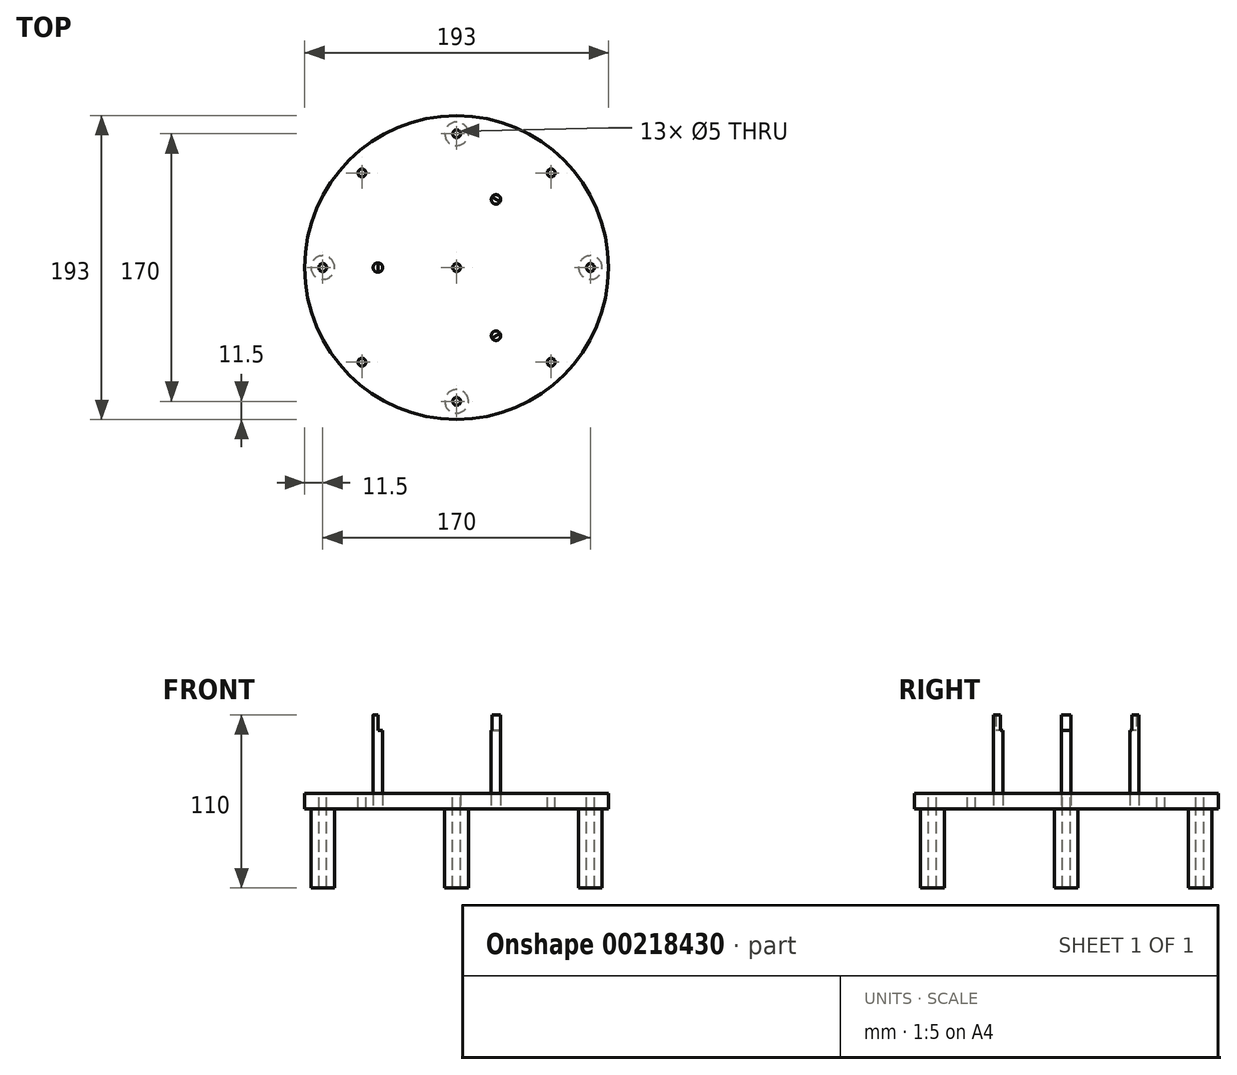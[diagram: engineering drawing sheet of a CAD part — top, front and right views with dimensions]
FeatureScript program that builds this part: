
annotation { "Feature Type Name" : "Feature", "Feature Type Description" : "" }
export const myFeature = defineFeature(function(context is Context, id is Id, definition is map)
    precondition{}
    {
        {
            var Q0;
            Q0=qCreatedBy(makeId("Front.planeOp"),FACE);
            var sketch = newSketch(context, id + "F0", { "sketchPlane" : qUnion([Q0])});
            skLineSegment(sketch, "E0", {"start": v(0, 0) * mm, "end": v(0, 66.09) * mm});
            skSolve(sketch);
        }
        {
            var Q0;
            Q0=qCreatedBy(makeId("Top.planeOp"),FACE);
            var sketch = newSketch(context, id + "F1", { "sketchPlane" : qUnion([Q0])});
            skCircle(sketch, "E1", {"center": v(0, 0) * mm, "radius": 96.5 * mm});
            skCircle(sketch, "E2.0", {"center": v(0, 0) * mm, "radius": 66.5 * mm});
            skCircle(sketch, "E3", {"center": v(0, 0) * mm, "radius": 63.5 * mm});
            skCircle(sketch, "E4", {"center": v(0, 0) * mm, "radius": 50 * mm});
            skCircle(sketch, "E5", {"center": v(0, 0) * mm, "radius": 47 * mm});
            skSolve(sketch);
        }
        {
            var Q0;
            Q0 = qSketchRegion(id + "F1", true);
            var Q1;
            Q1=makeQuery(id+"F1.imprint","IMPRINT",FACE,{"disambiguationData":[TD([[makeQuery(id+"F1.imprint","IMPRINT",EDGE,{"derivedFrom":sQuery(id+"F1.wireOp",EDGE,"E5")}),1.0]])]});
            var Q2;
            Q2=makeQuery(id+"F1.imprint","IMPRINT",FACE,{"disambiguationData":[TD([[makeQuery(id+"F1.imprint","IMPRINT",EDGE,{"derivedFrom":sQuery(id+"F1.wireOp",EDGE,"E4")}),1.0]])]});
            var Q3;
            Q3=makeQuery(id+"F1.imprint","IMPRINT",FACE,{"disambiguationData":[TD([[makeQuery(id+"F1.imprint","IMPRINT",EDGE,{"derivedFrom":sQuery(id+"F1.wireOp",EDGE,"E3")}),1.0]])]});
            var Q4;
            Q4=makeQuery(id+"F1.imprint","IMPRINT",FACE,{"disambiguationData":[TD([[makeQuery(id+"F1.imprint","IMPRINT",EDGE,{"derivedFrom":sQuery(id+"F1.wireOp",EDGE,"E2.0")}),1.0]])]});
            extrude(context, id + "F2", {"entities" : qUnion([Q0, Q1, Q2, Q3, Q4]), "depth" : 10 * mm});
        }
        {
            var Q0;
            Q0=qCreatedBy(makeId("Top.planeOp"),FACE);
            cPlane(context, id + "F3", {"entities" : qUnion([Q0]), "cplaneType" : CPlaneType.OFFSET, "offset" : 10 * mm, "width" : 150 * mm, "height" : 150 * mm});
        }
        {
            var Q0;
            Q0=qCreatedBy(id+"F3.planeOp",FACE);
            var sketch = newSketch(context, id + "F4", { "sketchPlane" : qUnion([Q0])});
            skCircle(sketch, "E6", {"center": v(-85, 0) * mm, "radius": 2.5 * mm});
            skSolve(sketch);
        }
        {
            var Q0;
            Q0=makeQuery(id+"F4.imprint","IMPRINT",FACE,{"disambiguationData":[TD([[makeQuery(id+"F4.imprint","IMPRINT",EDGE,{"derivedFrom":sQuery(id+"F4.wireOp",EDGE,"E6")}),1.0]])]});
            extrude(context, id + "F5", {"entities" : qUnion([Q0]), "oppositeDirection" : true, "depth" : 10 * mm});
        }
        {
            var Q0;
            Q0=makeQuery(id+"F5.opExtrude","SWEPT_BODY",BODY,{"disambiguationData":[OSD([sQuery(id+"F4.wireOp",EDGE,"E6")])]});
            var Q1;
            Q1=sQuery(id+"F0.wireOp",EDGE,"E0");
            circularPattern(context, id + "F6", {"entities" : qUnion([Q0]), "axis" : qUnion([Q1]), "angle" : 360 * degree, "instanceCount" : 8, "equalSpace" : true});
        }
        {
            var Q0;
            Q0=makeQuery(id+"F5.opExtrude","SWEPT_BODY",BODY,{"disambiguationData":[OSD([sQuery(id+"F4.wireOp",EDGE,"E6")])]});
            var Q1;
            Q1=makeQuery(id+"F6.opPattern","COPY",BODY,{"derivedFrom":makeQuery(id+"F5.opExtrude","SWEPT_BODY",BODY,{"disambiguationData":[OSD([sQuery(id+"F4.wireOp",EDGE,"E6")])]}),"instanceName":"7"});
            var Q2;
            Q2=makeQuery(id+"F6.opPattern","COPY",BODY,{"derivedFrom":makeQuery(id+"F5.opExtrude","SWEPT_BODY",BODY,{"disambiguationData":[OSD([sQuery(id+"F4.wireOp",EDGE,"E6")])]}),"instanceName":"6"});
            var Q3;
            Q3=makeQuery(id+"F6.opPattern","COPY",BODY,{"derivedFrom":makeQuery(id+"F5.opExtrude","SWEPT_BODY",BODY,{"disambiguationData":[OSD([sQuery(id+"F4.wireOp",EDGE,"E6")])]}),"instanceName":"5"});
            var Q4;
            Q4=makeQuery(id+"F6.opPattern","COPY",BODY,{"derivedFrom":makeQuery(id+"F5.opExtrude","SWEPT_BODY",BODY,{"disambiguationData":[OSD([sQuery(id+"F4.wireOp",EDGE,"E6")])]}),"instanceName":"4"});
            var Q5;
            Q5=makeQuery(id+"F6.opPattern","COPY",BODY,{"derivedFrom":makeQuery(id+"F5.opExtrude","SWEPT_BODY",BODY,{"disambiguationData":[OSD([sQuery(id+"F4.wireOp",EDGE,"E6")])]}),"instanceName":"3"});
            var Q6;
            Q6=makeQuery(id+"F6.opPattern","COPY",BODY,{"derivedFrom":makeQuery(id+"F5.opExtrude","SWEPT_BODY",BODY,{"disambiguationData":[OSD([sQuery(id+"F4.wireOp",EDGE,"E6")])]}),"instanceName":"2"});
            var Q7;
            Q7=makeQuery(id+"F6.opPattern","COPY",BODY,{"derivedFrom":makeQuery(id+"F5.opExtrude","SWEPT_BODY",BODY,{"disambiguationData":[OSD([sQuery(id+"F4.wireOp",EDGE,"E6")])]}),"instanceName":"1"});
            var Q8;
            Q8=makeQuery(id+"F2.opExtrude","SWEPT_BODY",BODY,{"disambiguationData":[OSD([sQuery(id+"F1.wireOp",EDGE,"E1")])]});
            booleanBodies(context, id + "F7", {"operationType" : BooleanOperationType.SUBTRACTION, "tools" : qUnion([Q0, Q1, Q2, Q3, Q4, Q5, Q6, Q7]), "targets" : qUnion([Q8])});
        }
        {
            var Q0;
            Q0=qCreatedBy(makeId("Top.planeOp"),FACE);
            var sketch = newSketch(context, id + "F8", { "sketchPlane" : qUnion([Q0])});
            skCircle(sketch, "E7", {"center": v(0, 0) * mm, "radius": 2.5 * mm});
            skSolve(sketch);
        }
        {
            var Q0;
            Q0 = qSketchRegion(id + "F8", true);
            extrude(context, id + "F9", {"entities" : qUnion([Q0]), "operationType" : NewBodyOperationType.REMOVE, "depth" : 10 * mm});
        }
        {
            var Q0;
            Q0=qCreatedBy(makeId("Top.planeOp"),FACE);
            var sketch = newSketch(context, id + "F10", { "sketchPlane" : qUnion([Q0])});
            skCircle(sketch, "E8", {"center": v(-85, 0) * mm, "radius": 2.5 * mm});
            skCircle(sketch, "E9.0", {"center": v(-85, 0) * mm, "radius": 7.5 * mm});
            skSolve(sketch);
        }
        {
            var Q0;
            Q0 = qSketchRegion(id + "F10", true);
            extrude(context, id + "F11", {"entities" : qUnion([Q0]), "oppositeDirection" : true, "depth" : 50 * mm});
        }
        {
            var Q0;
            Q0=makeQuery(id+"F11.opExtrude","SWEPT_BODY",BODY,{"disambiguationData":[OSD([sQuery(id+"F10.wireOp",EDGE,"E8"),sQuery(id+"F10.wireOp",EDGE,"E9.0")])]});
            var Q1;
            Q1=sQuery(id+"F0.wireOp",EDGE,"E0");
            circularPattern(context, id + "F12", {"entities" : qUnion([Q0]), "axis" : qUnion([Q1]), "angle" : 360 * degree, "instanceCount" : 4, "equalSpace" : true});
        }
        {
            var Q0;
            Q0=makeQuery(id+"F1.imprint","IMPRINT",FACE,{"disambiguationData":[TD([[makeQuery(id+"F1.imprint","IMPRINT",EDGE,{"derivedFrom":sQuery(id+"F1.wireOp",EDGE,"E1")}),1.0]])]});
            var sketch = newSketch(context, id + "F13", { "sketchPlane" : qUnion([Q0])});
            skCircle(sketch, "E10", {"center": v(-50, 0) * mm, "radius": 3 * mm});
            skSolve(sketch);
        }
        {
            var Q0;
            Q0=makeQuery(id+"F13.imprint","IMPRINT",FACE,{"disambiguationData":[TD([[makeQuery(id+"F13.imprint","IMPRINT",EDGE,{"derivedFrom":sQuery(id+"F13.wireOp",EDGE,"E10")}),1.0]])]});
            var Q1;
            Q1=sQuery(id+"F13.wireOp",EDGE,"E10");
            extrude(context, id + "F14", {"entities" : qUnion([Q0]), "surfaceEntities" : qUnion([Q1]), "depth" : 60 * mm});
        }
        {
            var Q0;
            Q0=qCreatedBy(makeId("Top.planeOp"),FACE);
            cPlane(context, id + "F15", {"entities" : qUnion([Q0]), "cplaneType" : CPlaneType.OFFSET, "offset" : 50 * mm, "width" : 150 * mm, "height" : 150 * mm});
        }
        {
            var Q0;
            Q0=makeQuery(id+"F14.opExtrude","SWEPT_BODY",BODY,{"disambiguationData":[OSD([sQuery(id+"F13.wireOp",EDGE,"E10")])]});
            var Q1;
            Q1=sQuery(id+"F0.wireOp",EDGE,"E0");
            circularPattern(context, id + "F16", {"entities" : qUnion([Q0]), "axis" : qUnion([Q1]), "angle" : 360 * degree, "instanceCount" : 3, "equalSpace" : true});
        }
        {
            var Q0;
            Q0=qCreatedBy(id+"F15.planeOp",FACE);
            var sketch = newSketch(context, id + "F17", { "sketchPlane" : qUnion([Q0])});
            skCircle(sketch, "E11", {"center": v(0, 0) * mm, "radius": 47 * mm});
            skCircle(sketch, "E12.0", {"center": v(0, 0) * mm, "radius": 50 * mm});
            skSolve(sketch);
        }
        {
            var Q0;
            Q0 = qSketchRegion(id + "F17", true);
            extrude(context, id + "F18", {"entities" : qUnion([Q0]), "operationType" : NewBodyOperationType.REMOVE, "depth" : 10 * mm});
        }
    });
